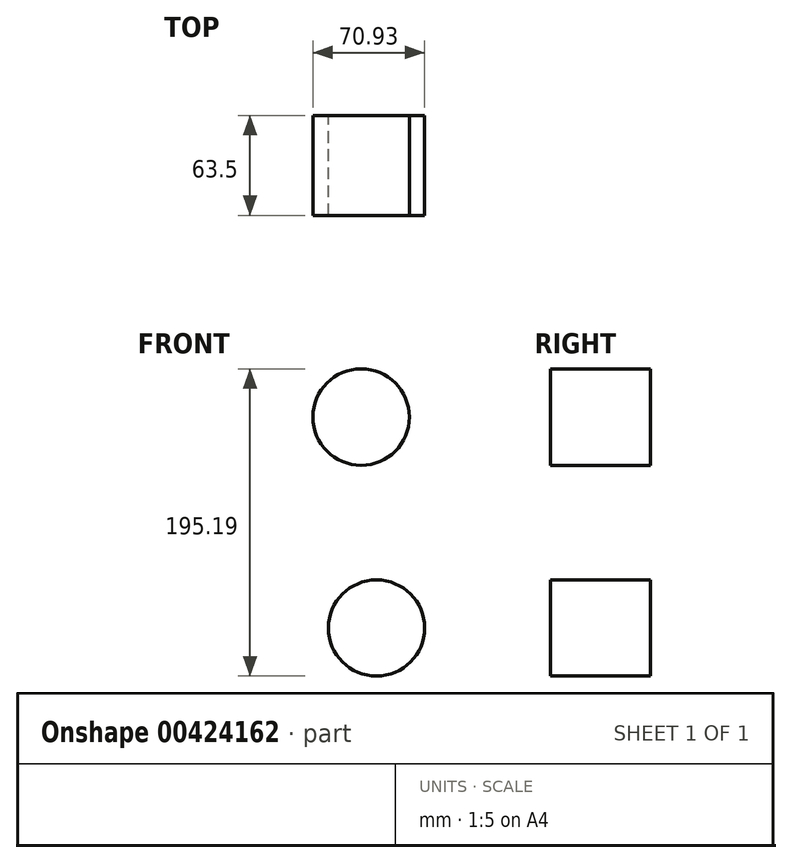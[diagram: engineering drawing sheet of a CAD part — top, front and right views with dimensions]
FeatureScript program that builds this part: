
annotation { "Feature Type Name" : "Feature", "Feature Type Description" : "" }
export const myFeature = defineFeature(function(context is Context, id is Id, definition is map)
    precondition{}
    {
        {
            var Q0;
            Q0=qCreatedBy(makeId("Front.planeOp"),FACE);
            var sketch = newSketch(context, id + "F0", { "sketchPlane" : qUnion([Q0])});
            skCircle(sketch, "E0", {"center": v(-150.13, 56.8) * mm, "radius": 30.65 * mm});
            skFitSpline(sketch, "E1", {"points": [v(-150.13, 56.8) * mm, v(-94.8, 0) * mm, v(-162.29, -9.33) * mm, v(-141.62, -78.14) * mm, v(-141.62, -77.53) * mm], "startDerivative": vector(293.9, -229.77) * mm, "endDerivative": vector(-7.9, 34.7) * mm});
            skSolve(sketch);
        }
        {
            var Q0;
            Q0=qCreatedBy(makeId("Front.planeOp"),FACE);
            var sketch = newSketch(context, id + "F1", { "sketchPlane" : qUnion([Q0])});
            skCircle(sketch, "E2", {"center": v(-140.4, -77.18) * mm, "radius": 30.55 * mm});
            skSolve(sketch);
        }
        {
            var Q0;
            Q0=makeQuery(id+"F0.imprint","IMPRINT",FACE,{"disambiguationData":[TD([[makeQuery(id+"F0.imprint","IMPRINT",EDGE,{"derivedFrom":sQuery(id+"F0.wireOp",EDGE,"E0")}),1.0]])]});
            var Q1;
            Q1=makeQuery(id+"F1.imprint","IMPRINT",FACE,{"disambiguationData":[TD([[makeQuery(id+"F1.imprint","IMPRINT",EDGE,{"derivedFrom":sQuery(id+"F1.wireOp",EDGE,"E2")}),1.0]])]});
            extrude(context, id + "F2", {"entities" : qUnion([Q0, Q1]), "depth" : 63.5 * mm});
        }
    });
